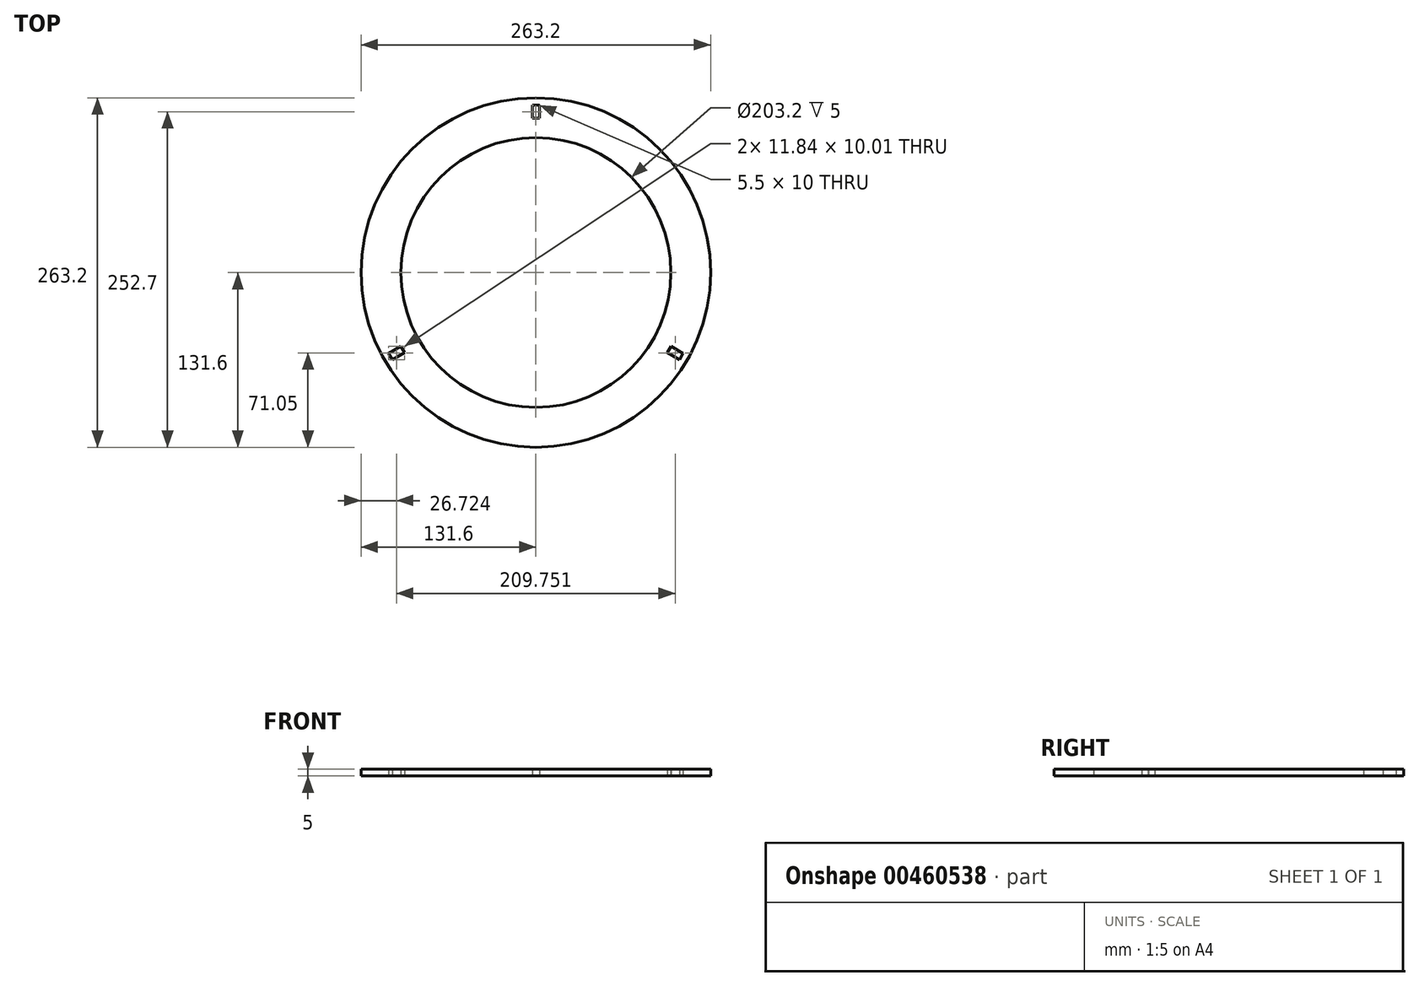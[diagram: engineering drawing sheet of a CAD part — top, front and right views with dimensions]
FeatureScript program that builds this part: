
annotation { "Feature Type Name" : "Feature", "Feature Type Description" : "" }
export const myFeature = defineFeature(function(context is Context, id is Id, definition is map)
    precondition{}
    {
        {
            var Q0;
            Q0=qCreatedBy(makeId("Top.planeOp"),FACE);
            var sketch = newSketch(context, id + "F0", { "sketchPlane" : qUnion([Q0])});
            skCircle(sketch, "E0", {"center": v(0, 0) * mm, "radius": 101.6 * mm});
            skCircle(sketch, "E1", {"center": v(0, 0) * mm, "radius": 131.6 * mm});
            skPoint(sketch, "E2", {"position": v(0, 101.6) * mm});
            skPoint(sketch, "E3", {"position": v(0, -101.6) * mm});
            skPoint(sketch, "E4", {"position": v(101.6, 0) * mm});
            skPoint(sketch, "E5", {"position": v(-101.6, 0) * mm});
            skPoint(sketch, "E6", {"position": v(131.6, 0) * mm});
            skPoint(sketch, "E7", {"position": v(0, 131.6) * mm});
            skPoint(sketch, "E8", {"position": v(-131.6, 0) * mm});
            skPoint(sketch, "E9", {"position": v(0, -131.6) * mm});
            skPoint(sketch, "E10", {"position": v(0, 121.1) * mm});
            skLineSegment(sketch, "E11.bottom", {"start": v(2.75, 116.1) * mm, "end": v(-2.75, 116.1) * mm});
            skLineSegment(sketch, "E11.top", {"start": v(2.75, 126.1) * mm, "end": v(-2.75, 126.1) * mm});
            skLineSegment(sketch, "E11.left", {"start": v(2.75, 116.1) * mm, "end": v(2.75, 126.1) * mm});
            skLineSegment(sketch, "E11.right", {"start": v(-2.75, 116.1) * mm, "end": v(-2.75, 126.1) * mm});
            skLineSegment(sketch, "E12", {"start": v(0, 0) * mm, "end": v(0, 121.1) * mm});
            skLineSegment(sketch, "E13", {"start": v(0, 0) * mm, "end": v(-104.88, -60.55) * mm});
            skLineSegment(sketch, "E14", {"start": v(0, 0) * mm, "end": v(104.88, -60.55) * mm});
            skPoint(sketch, "E15.middle", {"position": v(-104.88, -60.55) * mm});
            skLineSegment(sketch, "E16", {"start": v(-108.05, -65.56) * mm, "end": v(-110.8, -60.8) * mm});
            skLineSegment(sketch, "E17", {"start": v(-110.8, -60.8) * mm, "end": v(-101.7, -55.54) * mm});
            skLineSegment(sketch, "E18", {"start": v(-101.7, -55.54) * mm, "end": v(-98.95, -60.3) * mm});
            skLineSegment(sketch, "E19", {"start": v(-98.95, -60.3) * mm, "end": v(-108.05, -65.56) * mm});
            skPoint(sketch, "E20", {"position": v(-106.25, -58.17) * mm});
            skPoint(sketch, "E21", {"position": v(-103.5, -62.93) * mm});
            skLineSegment(sketch, "E22", {"start": v(-106.25, -58.17) * mm, "end": v(-103.5, -62.93) * mm, "construction": true});
            skPoint(sketch, "E23.MirrorP", {"position": v(103.5, -62.93) * mm});
            skLineSegment(sketch, "E24.MirrorCS", {"start": v(98.95, -60.3) * mm, "end": v(108.05, -65.56) * mm});
            skLineSegment(sketch, "E25.MirrorCS", {"start": v(110.8, -60.8) * mm, "end": v(101.7, -55.54) * mm});
            skLineSegment(sketch, "E26.MirrorCS", {"start": v(108.05, -65.56) * mm, "end": v(110.8, -60.8) * mm});
            skLineSegment(sketch, "E27.MirrorCS", {"start": v(101.7, -55.54) * mm, "end": v(98.95, -60.3) * mm});
            skPoint(sketch, "E28", {"position": v(-100.33, -57.92) * mm});
            skPoint(sketch, "E29", {"position": v(-91.45, -52.8) * mm});
            skSolve(sketch);
        }
        {
            var Q0;
            Q0=makeQuery(id+"F0.imprint","IMPRINT",FACE,{"disambiguationData":[TD([[makeQuery(id+"F0.imprint","IMPRINT",EDGE,{"derivedFrom":sQuery(id+"F0.wireOp",EDGE,"E0")}),-1.0]])]});
            extrude(context, id + "F1", {"entities" : qUnion([Q0]), "depth" : 5 * mm});
        }
    });
